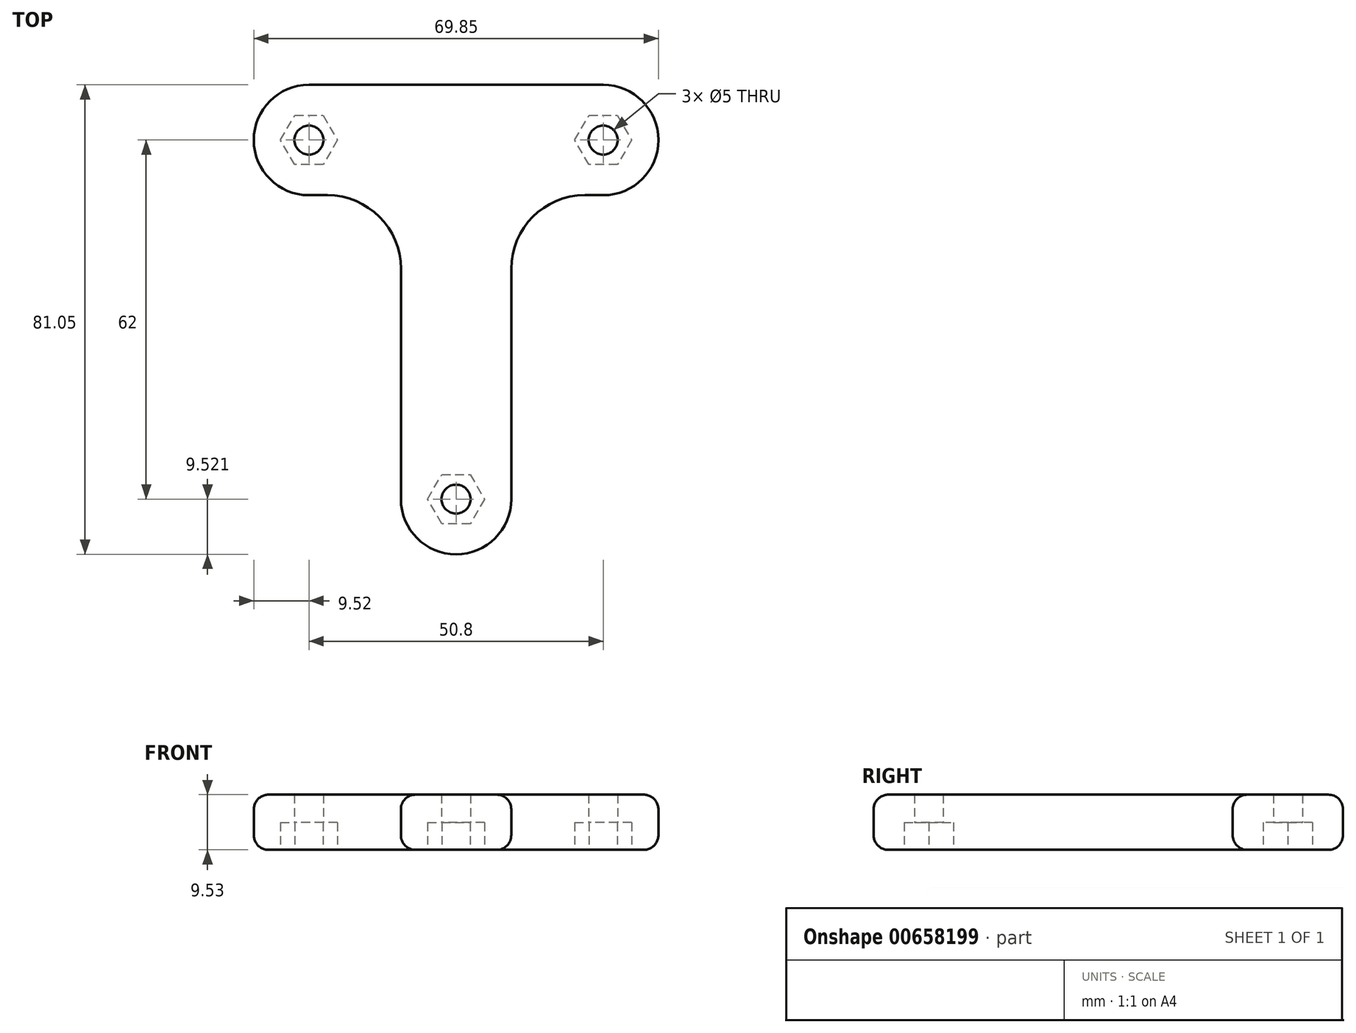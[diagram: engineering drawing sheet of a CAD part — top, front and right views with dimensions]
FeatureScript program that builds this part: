
annotation { "Feature Type Name" : "Feature", "Feature Type Description" : "" }
export const myFeature = defineFeature(function(context is Context, id is Id, definition is map)
    precondition{}
    {
        {
            var Q0;
            Q0=qCreatedBy(makeId("Top.planeOp"),FACE);
            var sketch = newSketch(context, id + "F0", { "sketchPlane" : qUnion([Q0])});
            skPoint(sketch, "E0.middle", {"position": v(0, 0) * mm});
            skLineSegment(sketch, "E1", {"start": v(-25.4, 29.26) * mm, "end": v(25.4, 29.26) * mm});
            skPoint(sketch, "E2", {"position": v(-25.4, 19.73) * mm});
            skPoint(sketch, "E3", {"position": v(25.4, 19.73) * mm});
            skPoint(sketch, "E4", {"position": v(0, -42.27) * mm});
            skCircle(sketch, "E5.cCircle", {"center": v(-25.4, 19.73) * mm, "radius": 4.25 * mm, "construction": true});
            skLineSegment(sketch, "E5.0", {"start": v(-22.95, 15.48) * mm, "end": v(-27.85, 15.48) * mm});
            skLineSegment(sketch, "E5.1", {"start": v(-27.85, 15.48) * mm, "end": v(-30.3, 19.73) * mm});
            skLineSegment(sketch, "E5.2", {"start": v(-30.3, 19.73) * mm, "end": v(-27.85, 23.98) * mm});
            skLineSegment(sketch, "E5.3", {"start": v(-27.85, 23.98) * mm, "end": v(-22.95, 23.98) * mm});
            skLineSegment(sketch, "E5.4", {"start": v(-22.95, 23.98) * mm, "end": v(-20.5, 19.73) * mm});
            skLineSegment(sketch, "E5.5", {"start": v(-20.5, 19.73) * mm, "end": v(-22.95, 15.48) * mm});
            skPoint(sketch, "E5.0.midPoint", {"position": v(-25.4, 15.48) * mm});
            skCircle(sketch, "E6.cCircle", {"center": v(25.4, 19.73) * mm, "radius": 4.25 * mm, "construction": true});
            skLineSegment(sketch, "E6.0", {"start": v(27.85, 15.48) * mm, "end": v(22.95, 15.48) * mm});
            skLineSegment(sketch, "E6.1", {"start": v(22.95, 15.48) * mm, "end": v(20.5, 19.73) * mm});
            skLineSegment(sketch, "E6.2", {"start": v(20.5, 19.73) * mm, "end": v(22.95, 23.98) * mm});
            skLineSegment(sketch, "E6.3", {"start": v(22.95, 23.98) * mm, "end": v(27.85, 23.98) * mm});
            skLineSegment(sketch, "E6.4", {"start": v(27.85, 23.98) * mm, "end": v(30.3, 19.73) * mm});
            skLineSegment(sketch, "E6.5", {"start": v(30.3, 19.73) * mm, "end": v(27.85, 15.48) * mm});
            skPoint(sketch, "E6.0.midPoint", {"position": v(25.4, 15.48) * mm});
            skCircle(sketch, "E7.cCircle", {"center": v(0, -42.27) * mm, "radius": 4.25 * mm, "construction": true});
            skLineSegment(sketch, "E7.0", {"start": v(-2.45, -38.02) * mm, "end": v(2.45, -38.02) * mm});
            skLineSegment(sketch, "E7.1", {"start": v(2.45, -38.02) * mm, "end": v(4.9, -42.27) * mm});
            skLineSegment(sketch, "E7.2", {"start": v(4.9, -42.27) * mm, "end": v(2.45, -46.52) * mm});
            skLineSegment(sketch, "E7.3", {"start": v(2.45, -46.52) * mm, "end": v(-2.45, -46.52) * mm});
            skLineSegment(sketch, "E7.4", {"start": v(-2.45, -46.52) * mm, "end": v(-4.9, -42.27) * mm});
            skLineSegment(sketch, "E7.5", {"start": v(-4.9, -42.27) * mm, "end": v(-2.45, -38.02) * mm});
            skPoint(sketch, "E7.0.midPoint", {"position": v(0, -38.02) * mm});
            skArc(sketch, "E8.MirrorC", {"start": v(25.4, 29.26) * mm, "mid": v(34.93, 19.73) * mm, "end": v(25.4, 10.2) * mm});
            skArc(sketch, "E9", {"start": v(-9.53, -42.27) * mm, "mid": v(0, -51.8) * mm, "end": v(9.53, -42.27) * mm});
            skLineSegment(sketch, "E10", {"start": v(9.53, -42.27) * mm, "end": v(9.53, -2.5) * mm});
            skLineSegment(sketch, "E11", {"start": v(25.4, 10.2) * mm, "end": v(22.23, 10.2) * mm});
            skPoint(sketch, "E12.visualSharp", {"position": v(9.53, 10.2) * mm});
            skArc(sketch, "E12.filletArc", {"start": v(22.23, 10.2) * mm, "mid": v(13.24, 6.49) * mm, "end": v(9.53, -2.5) * mm});
            skLineSegment(sketch, "E13.MirrorCS", {"start": v(-9.53, -42.27) * mm, "end": v(-9.53, -2.5) * mm});
            skArc(sketch, "E14.MirrorCS", {"start": v(-22.23, 10.2) * mm, "mid": v(-13.24, 6.49) * mm, "end": v(-9.53, -2.5) * mm});
            skLineSegment(sketch, "E15.MirrorCS", {"start": v(-25.4, 10.2) * mm, "end": v(-22.23, 10.2) * mm});
            skArc(sketch, "E16.MirrorCS", {"start": v(-25.4, 29.26) * mm, "mid": v(-34.93, 19.73) * mm, "end": v(-25.4, 10.2) * mm});
            skSolve(sketch);
        }
        {
            var Q0;
            Q0=makeQuery(id+"F0.imprint","IMPRINT",FACE,{"disambiguationData":[TD([[makeQuery(id+"F0.imprint","IMPRINT",EDGE,{"derivedFrom":sQuery(id+"F0.wireOp",EDGE,"E1")}),-1.0]])]});
            var Q1;
            Q1=makeQuery(id+"F0.imprint","IMPRINT",FACE,{"disambiguationData":[TD([[makeQuery(id+"F0.imprint","IMPRINT",EDGE,{"derivedFrom":sQuery(id+"F0.wireOp",EDGE,"E7.0")}),-1.0]])]});
            var Q2;
            Q2=makeQuery(id+"F0.imprint","IMPRINT",FACE,{"disambiguationData":[TD([[makeQuery(id+"F0.imprint","IMPRINT",EDGE,{"derivedFrom":sQuery(id+"F0.wireOp",EDGE,"E5.0")}),-1.0]])]});
            var Q3;
            Q3=makeQuery(id+"F0.imprint","IMPRINT",FACE,{"disambiguationData":[TD([[makeQuery(id+"F0.imprint","IMPRINT",EDGE,{"derivedFrom":sQuery(id+"F0.wireOp",EDGE,"E6.0")}),-1.0]])]});
            extrude(context, id + "F1", {"entities" : qUnion([Q0, Q1, Q2, Q3]), "depth" : 9.52 * mm, "offsetDistance" : 25.4 * mm});
        }
        {
            var Q0;
            Q0=sQuery(id+"F0.wireOp",VERTEX,"E3");
            var Q1;
            Q1=sQuery(id+"F0.wireOp",VERTEX,"E2");
            var Q2;
            Q2=sQuery(id+"F0.wireOp",VERTEX,"E4");
            var Q3;
            Q3=makeQuery(id+"F1.opExtrude","SWEPT_BODY",BODY,{"disambiguationData":[OSD([sQuery(id+"F0.wireOp",EDGE,"bDni5Pew-lR1S-mkra-pztY-FT0CmZDIweA1"),sQuery(id+"F0.wireOp",EDGE,"c15fabfa-4c59-493d-87ff-b9c6b254ed6b0.MirrorC"),sQuery(id+"F0.wireOp",EDGE,"EvyleWwj-wpsp-KnVs-EkhO-14JM1m7kGcU1"),sQuery(id+"F0.wireOp",EDGE,"WeK0TyH7-iKCF-Q6uN-zMjH-say8fqwKQ1SW"),sQuery(id+"F0.wireOp",EDGE,"2FkoO6pD-tnLh-C9xh-j56a-zK0mz5MqNUJC"),sQuery(id+"F0.wireOp",EDGE,"E1")])]});
            hole(context, id + "F2", {"style" : HoleStyle.SIMPLE, "endStyle" : HoleEndStyle.THROUGH, "oppositeDirection" : true, "standardTappedOrClearance" : lookupTablePath({ "standard" : "ISO", "size" : "5", "type" : "Drilled" }), "standardBlindInLast" : lookupTablePath({ "standard" : "ISO", "size" : "5", "type" : "Drilled" }), "holeDiameter" : 5 * mm, "majorDiameter" : 6.35 * mm, "isTappedThrough" : true, "tappedDepth" : 12.7 * mm, "tapClearance" : 3, "locations" : qUnion([Q0, Q1, Q2]), "scope" : qUnion([Q3])});
        }
        {
            var Q0;
            Q0=makeQuery(id+"F1.opExtrude","CAP_EDGE",EDGE,{"disambiguationData":[OSD([sQuery(id+"F0.wireOp",EDGE,"E1")])],"isStart":true});
            var Q1;
            Q1=makeQuery(id+"F1.opExtrude","CAP_EDGE",EDGE,{"disambiguationData":[OSD([sQuery(id+"F0.wireOp",EDGE,"6ff57d8d-353b-45d4-9937-0f36a12270d6.0")])],"isStart":true});
            var Q2;
            Q2=makeQuery(id+"F1.opExtrude","CAP_EDGE",EDGE,{"disambiguationData":[OSD([sQuery(id+"F0.wireOp",EDGE,"E1")])],"isStart":false});
            var Q3;
            Q3=makeQuery(id+"F1.opExtrude","CAP_EDGE",EDGE,{"disambiguationData":[OSD([sQuery(id+"F0.wireOp",EDGE,"6ff57d8d-353b-45d4-9937-0f36a12270d6.0")])],"isStart":false});
            fillet(context, id + "F3", {"entities" : qUnion([Q0, Q1, Q2, Q3]), "radius" : 2.54 * mm, "tangentPropagation" : true, "allowEdgeOverflow" : false});
        }
        {
            var Q0;
            Q0=makeQuery(id+"F0.imprint","IMPRINT",FACE,{"disambiguationData":[TD([[makeQuery(id+"F0.imprint","IMPRINT",EDGE,{"derivedFrom":sQuery(id+"F0.wireOp",EDGE,"E7.0")}),-1.0]])]});
            var Q1;
            Q1=makeQuery(id+"F0.imprint","IMPRINT",FACE,{"disambiguationData":[TD([[makeQuery(id+"F0.imprint","IMPRINT",EDGE,{"derivedFrom":sQuery(id+"F0.wireOp",EDGE,"E5.0")}),-1.0]])]});
            var Q2;
            Q2=makeQuery(id+"F0.imprint","IMPRINT",FACE,{"disambiguationData":[TD([[makeQuery(id+"F0.imprint","IMPRINT",EDGE,{"derivedFrom":sQuery(id+"F0.wireOp",EDGE,"E6.0")}),-1.0]])]});
            extrude(context, id + "F4", {"entities" : qUnion([Q0, Q1, Q2]), "operationType" : NewBodyOperationType.REMOVE, "depth" : 4.7 * mm, "offsetDistance" : 25.4 * mm});
        }
    });
